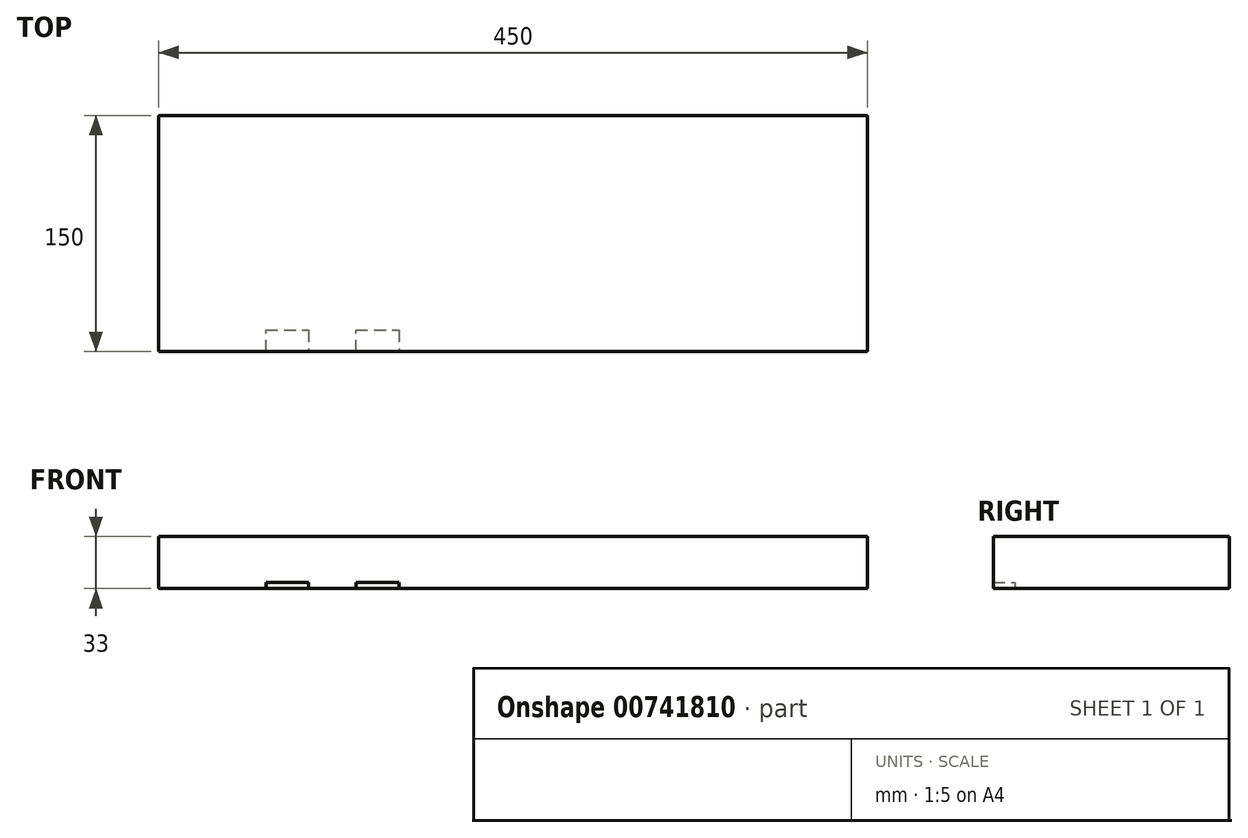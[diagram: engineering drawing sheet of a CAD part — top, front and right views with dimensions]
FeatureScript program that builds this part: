
annotation { "Feature Type Name" : "Feature", "Feature Type Description" : "" }
export const myFeature = defineFeature(function(context is Context, id is Id, definition is map)
    precondition{}
    {
        {
            var Q0;
            Q0=qCreatedBy(makeId("Top.planeOp"),FACE);
            var sketch = newSketch(context, id + "F0", { "sketchPlane" : qUnion([Q0])});
            skLineSegment(sketch, "E0.bottom", {"start": v(-220.8, 51.3) * mm, "end": v(229.2, 51.3) * mm});
            skLineSegment(sketch, "E0.top", {"start": v(-220.8, -98.7) * mm, "end": v(229.2, -98.7) * mm});
            skLineSegment(sketch, "E0.left", {"start": v(-220.8, 51.3) * mm, "end": v(-220.8, -98.7) * mm});
            skLineSegment(sketch, "E0.right", {"start": v(229.2, 51.3) * mm, "end": v(229.2, -98.7) * mm});
            skLineSegment(sketch, "E1", {"start": v(-152.8, -98.7) * mm, "end": v(-152.8, -85.1) * mm});
            skLineSegment(sketch, "E2", {"start": v(-152.8, -85.1) * mm, "end": v(-125.6, -85.1) * mm});
            skLineSegment(sketch, "E3", {"start": v(-125.6, -85.1) * mm, "end": v(-125.6, -98.7) * mm});
            skLineSegment(sketch, "E4", {"start": v(-125.6, -98.7) * mm, "end": v(-95.6, -98.7) * mm});
            skLineSegment(sketch, "E5", {"start": v(-95.6, -98.7) * mm, "end": v(-95.6, -85.1) * mm});
            skLineSegment(sketch, "E6", {"start": v(-95.6, -85.1) * mm, "end": v(-68.4, -85.1) * mm});
            skLineSegment(sketch, "E7", {"start": v(-68.4, -85.1) * mm, "end": v(-68.4, -98.7) * mm});
            skSolve(sketch);
        }
        {
            var Q0;
            {var subQ0=sQuery(id+"F0.wireOp",EDGE,"E1");Q0=makeQuery(id+"F0.imprint","IMPRINT",FACE,{"disambiguationData":[TD([[makeQuery(id+"F0.imprint","IMPRINT",EDGE,{"derivedFrom":subQ0}),-1.0]])]});}
            var Q1;
            {var subQ0=sQuery(id+"F0.wireOp",EDGE,"E5");Q1=makeQuery(id+"F0.imprint","IMPRINT",FACE,{"disambiguationData":[TD([[makeQuery(id+"F0.imprint","IMPRINT",EDGE,{"derivedFrom":subQ0}),-1.0]])]});}
            extrude(context, id + "F1", {"entities" : qUnion([Q0, Q1]), "depth" : 3.8 * mm, "offsetDistance" : 25 * mm});
        }
        {
            var Q0;
            Q0=qSketchRegion(id+"F0",true);
            extrude(context, id + "F2", {"entities" : qUnion([Q0]), "depth" : 33 * mm, "offsetDistance" : 25 * mm});
        }
        {
            var Q0;
            Q0=makeQuery(id+"F1.opExtrude","SWEPT_BODY",BODY,{"disambiguationData":[OSD([sQuery(id+"F0.wireOp",EDGE,"E0.top"),sQuery(id+"F0.wireOp",EDGE,"E1"),sQuery(id+"F0.wireOp",EDGE,"E2"),sQuery(id+"F0.wireOp",EDGE,"E3")])]});
            var Q1;
            Q1=makeQuery(id+"F1.opExtrude","SWEPT_BODY",BODY,{"disambiguationData":[OSD([sQuery(id+"F0.wireOp",EDGE,"E0.top"),sQuery(id+"F0.wireOp",EDGE,"E5"),sQuery(id+"F0.wireOp",EDGE,"E6"),sQuery(id+"F0.wireOp",EDGE,"E7")])]});
            var Q2;
            Q2=makeQuery(id+"F2.opExtrude","SWEPT_BODY",BODY,{"disambiguationData":[OSD([sQuery(id+"F0.wireOp",EDGE,"E0.bottom"),sQuery(id+"F0.wireOp",EDGE,"E0.top"),sQuery(id+"F0.wireOp",EDGE,"E0.left"),sQuery(id+"F0.wireOp",EDGE,"E0.right"),sQuery(id+"F0.wireOp",EDGE,"E4")])]});
            booleanBodies(context, id + "F3", {"operationType" : BooleanOperationType.SUBTRACTION, "tools" : qUnion([Q0, Q1]), "targets" : qUnion([Q2])});
        }
    });
